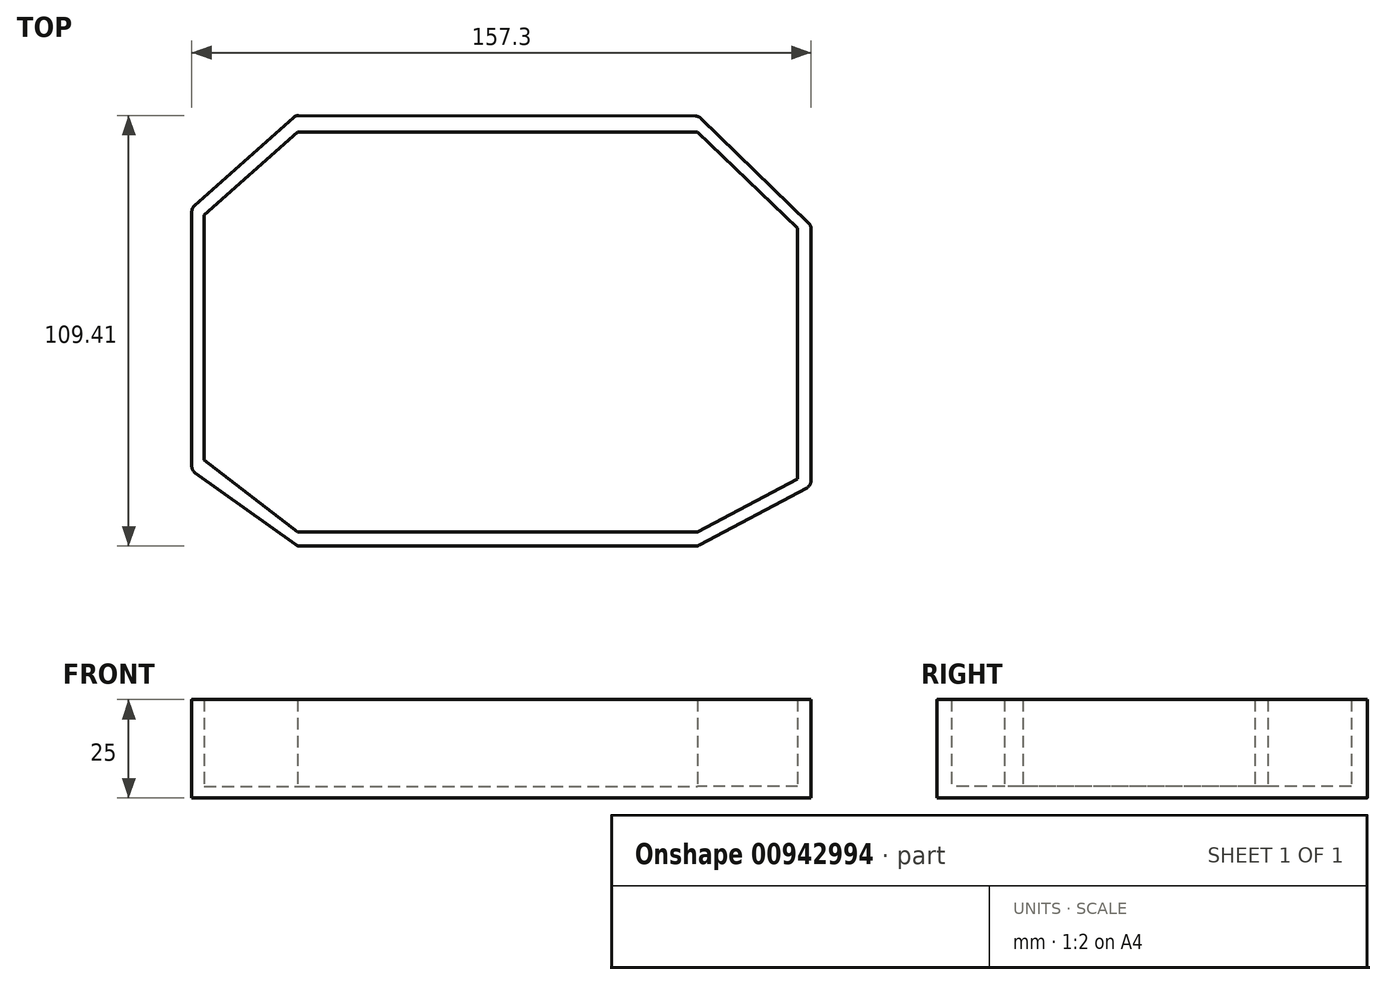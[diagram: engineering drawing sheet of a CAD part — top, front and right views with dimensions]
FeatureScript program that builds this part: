
annotation { "Feature Type Name" : "Feature", "Feature Type Description" : "" }
export const myFeature = defineFeature(function(context is Context, id is Id, definition is map)
    precondition{}
    {
        {
            var Q0;
            Q0=qCreatedBy(makeId("Top.planeOp"),FACE);
            var sketch = newSketch(context, id + "F0", { "sketchPlane" : qUnion([Q0])});
            skLineSegment(sketch, "E0.bottom", {"start": v(-50.8, 50.8) * mm, "end": v(50.8, 50.8) * mm});
            skLineSegment(sketch, "E0.top", {"start": v(-50.8, -50.8) * mm, "end": v(50.8, -50.8) * mm});
            skLineSegment(sketch, "E0.left", {"start": v(-50.8, 50.8) * mm, "end": v(-50.8, -50.8) * mm});
            skLineSegment(sketch, "E0.right", {"start": v(50.8, 50.8) * mm, "end": v(50.8, -50.8) * mm});
            skPoint(sketch, "E0.middle", {"position": v(0, 0) * mm});
            skLineSegment(sketch, "E1", {"start": v(-50.8, 50.8) * mm, "end": v(-74.55, 29.66) * mm});
            skLineSegment(sketch, "E2", {"start": v(-74.55, 29.66) * mm, "end": v(-74.55, -32.54) * mm});
            skLineSegment(sketch, "E3", {"start": v(-74.55, -32.54) * mm, "end": v(-50.8, -50.8) * mm});
            skLineSegment(sketch, "E4", {"start": v(50.8, 50.8) * mm, "end": v(76.22, 26.39) * mm});
            skLineSegment(sketch, "E5", {"start": v(76.22, 26.39) * mm, "end": v(76.22, -37.33) * mm});
            skLineSegment(sketch, "E6", {"start": v(76.22, -37.33) * mm, "end": v(50.8, -50.8) * mm});
            skLineSegment(sketch, "E7", {"start": v(-77.69, 31.45) * mm, "end": v(-77.69, -35.2) * mm});
            skLineSegment(sketch, "E8", {"start": v(-77.69, -35.2) * mm, "end": v(-50.8, -54.43) * mm});
            skLineSegment(sketch, "E9", {"start": v(-50.8, -54.43) * mm, "end": v(50.8, -54.43) * mm});
            skLineSegment(sketch, "E10", {"start": v(50.8, -54.43) * mm, "end": v(79.61, -39.05) * mm});
            skLineSegment(sketch, "E11", {"start": v(79.61, -39.05) * mm, "end": v(79.61, 27.06) * mm});
            skLineSegment(sketch, "E12", {"start": v(79.61, 27.06) * mm, "end": v(51.14, 54.81) * mm});
            skLineSegment(sketch, "E13", {"start": v(-77.69, 31.45) * mm, "end": v(-51.3, 54.98) * mm});
            skLineSegment(sketch, "E14", {"start": v(-51.3, 54.98) * mm, "end": v(51.14, 54.81) * mm});
            skSolve(sketch);
        }
        {
            var Q0;
            Q0=makeQuery(id+"F0.imprint","IMPRINT",FACE,{"disambiguationData":[TD([[makeQuery(id+"F0.imprint","IMPRINT",EDGE,{"derivedFrom":sQuery(id+"F0.wireOp",EDGE,"E0.left")}),-1.0]])]});
            var Q1;
            Q1=makeQuery(id+"F0.imprint","IMPRINT",FACE,{"disambiguationData":[TD([[makeQuery(id+"F0.imprint","IMPRINT",EDGE,{"derivedFrom":sQuery(id+"F0.wireOp",EDGE,"E0.bottom")}),-1.0]])]});
            var Q2;
            Q2=makeQuery(id+"F0.imprint","IMPRINT",FACE,{"disambiguationData":[TD([[makeQuery(id+"F0.imprint","IMPRINT",EDGE,{"derivedFrom":sQuery(id+"F0.wireOp",EDGE,"E0.right")}),1.0]])]});
            extrude(context, id + "F1", {"entities" : qUnion([Q0, Q1, Q2]), "depth" : 3 * mm, "offsetDistance" : 25 * mm});
        }
        {
            var Q0;
            Q0=makeQuery(id+"F0.imprint","IMPRINT",FACE,{"disambiguationData":[TD([[makeQuery(id+"F0.imprint","IMPRINT",EDGE,{"derivedFrom":sQuery(id+"F0.wireOp",EDGE,"E0.bottom")}),1.0]])]});
            extrude(context, id + "F2", {"entities" : qUnion([Q0]), "operationType" : NewBodyOperationType.ADD, "depth" : 25 * mm, "offsetDistance" : 25 * mm});
        }
        {
            var Q0;
            Q0=makeQuery(id+"F2.opExtrude","SWEPT_EDGE",EDGE,{"disambiguationData":[OSD([sQuery(id+"F0.wireOp",EDGE,"E8"),sQuery(id+"F0.wireOp",EDGE,"E9")])]});
            var Q1;
            Q1=makeQuery(id+"F2.opExtrude","SWEPT_EDGE",EDGE,{"disambiguationData":[OSD([sQuery(id+"F0.wireOp",EDGE,"E7"),sQuery(id+"F0.wireOp",EDGE,"E8")])]});
            var Q2;
            Q2=makeQuery(id+"F2.opExtrude","SWEPT_EDGE",EDGE,{"disambiguationData":[OSD([sQuery(id+"F0.wireOp",EDGE,"E9"),sQuery(id+"F0.wireOp",EDGE,"E10")])]});
            var Q3;
            Q3=makeQuery(id+"F2.opExtrude","SWEPT_EDGE",EDGE,{"disambiguationData":[OSD([sQuery(id+"F0.wireOp",EDGE,"E10"),sQuery(id+"F0.wireOp",EDGE,"E11")])]});
            var Q4;
            Q4=makeQuery(id+"F2.opExtrude","SWEPT_EDGE",EDGE,{"disambiguationData":[OSD([sQuery(id+"F0.wireOp",EDGE,"E11"),sQuery(id+"F0.wireOp",EDGE,"E12")])]});
            var Q5;
            Q5=makeQuery(id+"F2.opExtrude","SWEPT_EDGE",EDGE,{"disambiguationData":[OSD([sQuery(id+"F0.wireOp",EDGE,"E12"),sQuery(id+"F0.wireOp",EDGE,"E14")])]});
            var Q6;
            Q6=makeQuery(id+"F2.opExtrude","SWEPT_EDGE",EDGE,{"disambiguationData":[OSD([sQuery(id+"F0.wireOp",EDGE,"E13"),sQuery(id+"F0.wireOp",EDGE,"E14")])]});
            var Q7;
            Q7=makeQuery(id+"F2.opExtrude","SWEPT_EDGE",EDGE,{"disambiguationData":[OSD([sQuery(id+"F0.wireOp",EDGE,"E7"),sQuery(id+"F0.wireOp",EDGE,"E13")])]});
            fillet(context, id + "F3", {"entities" : qUnion([Q0, Q1, Q2, Q3, Q4, Q5, Q6, Q7]), "radius" : 2 * mm, "tangentPropagation" : true, "allowEdgeOverflow" : false});
        }
    });
